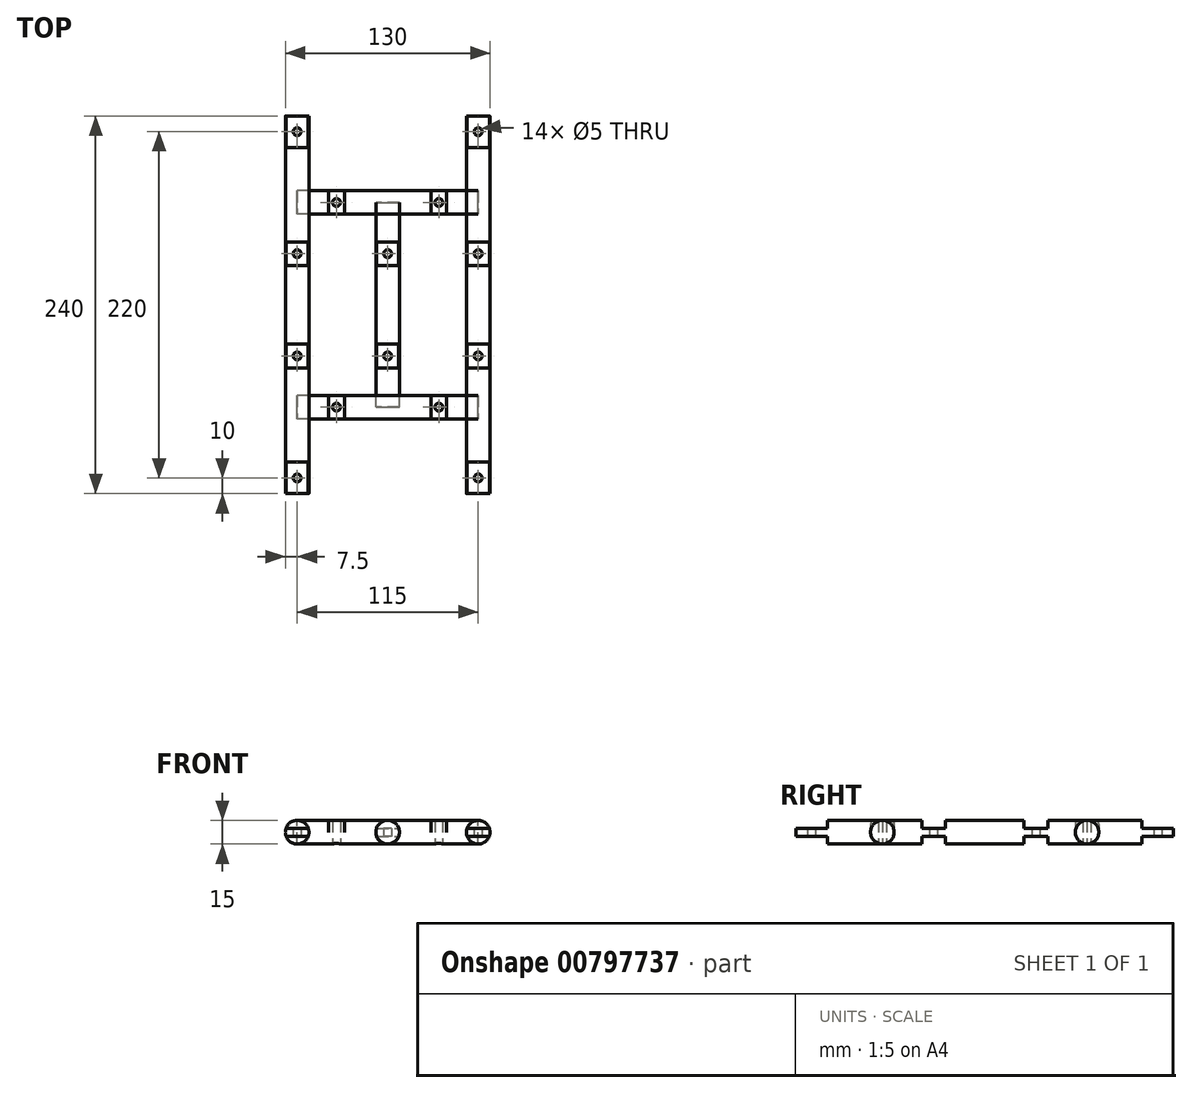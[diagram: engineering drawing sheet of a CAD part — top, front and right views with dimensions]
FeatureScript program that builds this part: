
annotation { "Feature Type Name" : "Feature", "Feature Type Description" : "" }
export const myFeature = defineFeature(function(context is Context, id is Id, definition is map)
    precondition{}
    {
        {
            var Q0;
            Q0=qCreatedBy(makeId("Top.planeOp"),FACE);
            var sketch = newSketch(context, id + "F0", { "sketchPlane" : qUnion([Q0])});
            skLineSegment(sketch, "E0.bottom", {"start": v(-65, 120) * mm, "end": v(-50, 120) * mm});
            skLineSegment(sketch, "E0.top", {"start": v(-65, -120) * mm, "end": v(-50, -120) * mm});
            skLineSegment(sketch, "E0.left", {"start": v(-65, 120) * mm, "end": v(-65, -120) * mm});
            skLineSegment(sketch, "E0.right", {"start": v(-50, 120) * mm, "end": v(-50, 65) * mm});
            skLineSegment(sketch, "E1.MirrorCS", {"start": v(65, 120) * mm, "end": v(50, 120) * mm});
            skLineSegment(sketch, "E2.MirrorCS", {"start": v(65, -120) * mm, "end": v(50, -120) * mm});
            skLineSegment(sketch, "E3.MirrorCS", {"start": v(65, 120) * mm, "end": v(65, -120) * mm});
            skLineSegment(sketch, "E4.MirrorCS", {"start": v(50, 120) * mm, "end": v(50, 65) * mm});
            skLineSegment(sketch, "E5.bottom", {"start": v(-50, -50) * mm, "end": v(50, -50) * mm});
            skLineSegment(sketch, "E5.top", {"start": v(-50, -65) * mm, "end": v(50, -65) * mm});
            skLineSegment(sketch, "E6.bottom", {"start": v(-50, 65) * mm, "end": v(50, 65) * mm});
            skLineSegment(sketch, "E6.top", {"start": v(-50, 50) * mm, "end": v(50, 50) * mm});
            skLineSegment(sketch, "E7", {"start": v(-57.5, -120) * mm, "end": v(-57.5, 120) * mm, "construction": true});
            skLineSegment(sketch, "E8", {"start": v(-50, -57.5) * mm, "end": v(50, -57.5) * mm, "construction": true});
            skLineSegment(sketch, "E9", {"start": v(-50, 57.5) * mm, "end": v(50, 57.5) * mm, "construction": true});
            skLineSegment(sketch, "E10", {"start": v(57.5, 120) * mm, "end": v(57.5, -120) * mm, "construction": true});
            skLineSegment(sketch, "E11.trimOffspring", {"start": v(-50, -65) * mm, "end": v(-50, -120) * mm});
            skLineSegment(sketch, "E12.trimOffspring", {"start": v(50, -65) * mm, "end": v(50, -120) * mm});
            skLineSegment(sketch, "E13.trimOffspring", {"start": v(-50, 50) * mm, "end": v(-50, -50) * mm});
            skLineSegment(sketch, "E14.trimOffspring", {"start": v(50, 50) * mm, "end": v(50, -50) * mm});
            skLineSegment(sketch, "E15", {"start": v(-57.5, 120) * mm, "end": v(57.5, 120) * mm, "construction": true});
            skLineSegment(sketch, "E16", {"start": v(-57.5, -120) * mm, "end": v(57.5, -120) * mm, "construction": true});
            skLineSegment(sketch, "E17", {"start": v(0, -120) * mm, "end": v(0, 120) * mm, "construction": true});
            skLineSegment(sketch, "E18.bottom", {"start": v(-7.5, -57.5) * mm, "end": v(7.5, -57.5) * mm});
            skLineSegment(sketch, "E18.top", {"start": v(-7.5, 57.5) * mm, "end": v(7.5, 57.5) * mm});
            skLineSegment(sketch, "E18.left", {"start": v(-7.5, -57.5) * mm, "end": v(-7.5, 57.5) * mm});
            skLineSegment(sketch, "E18.right", {"start": v(7.5, -57.5) * mm, "end": v(7.5, 57.5) * mm});
            skSolve(sketch);
        }
        {
            var Q0;
            {var subQ1=sQuery(id+"F0.wireOp",EDGE,"E0.bottom");Q0=makeQuery(id+"F0.imprint","IMPRINT",FACE,{"disambiguationData":[TD([[makeQuery(id+"F0.imprint","IMPRINT",EDGE,{"derivedFrom":subQ1}),-1.0]])]});}
            var Q1;
            Q1=makeQuery(id+"F0.imprint","IMPRINT",FACE,{"disambiguationData":[TD([[makeQuery(id+"F0.imprint","IMPRINT",EDGE,{"derivedFrom":sQuery(id+"F0.wireOp",EDGE,"E5.bottom")}),-1.0]])]});
            var Q2;
            {var subQ1=sQuery(id+"F0.wireOp",EDGE,"E1.MirrorCS");Q2=makeQuery(id+"F0.imprint","IMPRINT",FACE,{"disambiguationData":[TD([[makeQuery(id+"F0.imprint","IMPRINT",EDGE,{"derivedFrom":subQ1}),1.0]])]});}
            var Q3;
            Q3=makeQuery(id+"F0.imprint","IMPRINT",FACE,{"disambiguationData":[TD([[makeQuery(id+"F0.imprint","IMPRINT",EDGE,{"derivedFrom":sQuery(id+"F0.wireOp",EDGE,"E6.bottom")}),-1.0]])]});
            var Q4;
            {var subQ0=sQuery(id+"F0.wireOp",EDGE,"E18.left");var subQ1=sQuery(id+"F0.wireOp",EDGE,"E5.bottom");var subQ2=makeQuery(id+"F0.imprint","INTERSECT",VERTEX,{"derivedFrom":[subQ1,subQ0]});Q4=makeQuery(id+"F0.imprint","IMPRINT",FACE,{"disambiguationData":[TD([[makeQuery(id+"F0.imprint","IMPRINT",EDGE,{"disambiguationData":[TD([[subQ2,-1.0]])],"derivedFrom":subQ1}),1.0]])]});}
            var Q5;
            {var subQ5=sQuery(id+"F0.wireOp",EDGE,"E18.bottom");Q5=makeQuery(id+"F0.imprint","IMPRINT",FACE,{"disambiguationData":[TD([[makeQuery(id+"F0.imprint","IMPRINT",EDGE,{"derivedFrom":subQ5}),1.0]])]});}
            var Q6;
            {var subQ5=sQuery(id+"F0.wireOp",EDGE,"E18.top");Q6=makeQuery(id+"F0.imprint","IMPRINT",FACE,{"disambiguationData":[TD([[makeQuery(id+"F0.imprint","IMPRINT",EDGE,{"derivedFrom":subQ5}),-1.0]])]});}
            extrude(context, id + "F1", {"entities" : qUnion([Q0, Q1, Q2, Q3, Q4, Q5, Q6]), "depth" : 15 * mm, "offsetDistance" : 25 * mm});
        }
        {
            var Q0;
            Q0=qCreatedBy(makeId("Front.planeOp"),FACE);
            var sketch = newSketch(context, id + "F2", { "sketchPlane" : qUnion([Q0])});
            skLineSegment(sketch, "E19", {"start": v(0, 0) * mm, "end": v(57.99, 0) * mm, "construction": true});
            skLineSegment(sketch, "E20", {"start": v(0, 0) * mm, "end": v(0, 15) * mm, "construction": true});
            skLineSegment(sketch, "E21", {"start": v(-57.5, 7.5) * mm, "end": v(0, 7.5) * mm, "construction": true});
            skPoint(sketch, "E21.startSnap0", {"position": v(0, 7.5) * mm});
            skLineSegment(sketch, "E22", {"start": v(0, 7.5) * mm, "end": v(57.5, 7.5) * mm, "construction": true});
            skCircle(sketch, "E23", {"center": v(-57.5, 7.5) * mm, "radius": 7.5 * mm});
            skCircle(sketch, "E24", {"center": v(57.5, 7.5) * mm, "radius": 7.5 * mm});
            skCircle(sketch, "E25", {"center": v(0, 7.5) * mm, "radius": 7.5 * mm});
            skSolve(sketch);
        }
        {
            var Q0;
            Q0 = qSketchRegion(id + "F2", true);
            extrude(context, id + "F3", {"entities" : qUnion([Q0]), "operationType" : NewBodyOperationType.INTERSECT, "depth" : 125 * mm, "offsetDistance" : 25 * mm, "hasSecondDirection" : true, "secondDirectionOppositeDirection" : true, "secondDirectionDepth" : 125 * mm});
        }
        {
            var Q0;
            Q0=qCreatedBy(makeId("Right.planeOp"),FACE);
            var sketch = newSketch(context, id + "F4", { "sketchPlane" : qUnion([Q0])});
            skLineSegment(sketch, "E26", {"start": v(0, 0) * mm, "end": v(0, 15) * mm, "construction": true});
            skLineSegment(sketch, "E27", {"start": v(0, 7.5) * mm, "end": v(65, 7.5) * mm, "construction": true});
            skLineSegment(sketch, "E28", {"start": v(0, 7.5) * mm, "end": v(-65, 7.5) * mm, "construction": true});
            skCircle(sketch, "E29", {"center": v(65, 7.5) * mm, "radius": 7.5 * mm});
            skCircle(sketch, "E30", {"center": v(-65, 7.5) * mm, "radius": 7.5 * mm});
            skSolve(sketch);
        }
        {
            var Q0;
            Q0=makeQuery(id+"F4.imprint","IMPRINT",FACE,{"disambiguationData":[TD([[makeQuery(id+"F4.imprint","IMPRINT",EDGE,{"derivedFrom":sQuery(id+"F4.wireOp",EDGE,"E29")}),1.0]])]});
            var Q1;
            Q1=makeQuery(id+"F4.imprint","IMPRINT",FACE,{"disambiguationData":[TD([[makeQuery(id+"F4.imprint","IMPRINT",EDGE,{"derivedFrom":sQuery(id+"F4.wireOp",EDGE,"E30")}),1.0]])]});
            extrude(context, id + "F5", {"entities" : qUnion([Q0, Q1]), "depth" : 57.5 * mm, "offsetDistance" : 25 * mm, "hasSecondDirection" : true, "secondDirectionOppositeDirection" : true, "secondDirectionDepth" : 57.5 * mm});
        }
        {
            var Q0;
            Q0=qCreatedBy(makeId("Right.planeOp"),FACE);
            var sketch = newSketch(context, id + "F6", { "sketchPlane" : qUnion([Q0])});
            skLineSegment(sketch, "E31", {"start": v(0, 0) * mm, "end": v(0, 15) * mm, "construction": true});
            skLineSegment(sketch, "E32", {"start": v(120, 7.5) * mm, "end": v(-120, 7.5) * mm, "construction": true});
            skPoint(sketch, "E32.startSnap0", {"position": v(0, 7.5) * mm});
            skPoint(sketch, "E33", {"position": v(-110, 7.5) * mm});
            skPoint(sketch, "E34", {"position": v(-32.5, 7.5) * mm});
            skPoint(sketch, "E35", {"position": v(32.5, 7.5) * mm});
            skPoint(sketch, "E36", {"position": v(110, 7.5) * mm});
            skLineSegment(sketch, "E37.bottom", {"start": v(120, 10) * mm, "end": v(100, 10) * mm});
            skLineSegment(sketch, "E37.top", {"start": v(120, 5) * mm, "end": v(100, 5) * mm});
            skLineSegment(sketch, "E38.bottom", {"start": v(40, 10) * mm, "end": v(25, 10) * mm});
            skLineSegment(sketch, "E38.top", {"start": v(40, 5) * mm, "end": v(25, 5) * mm});
            skLineSegment(sketch, "E39.bottom", {"start": v(-25, 10) * mm, "end": v(-40, 10) * mm});
            skLineSegment(sketch, "E39.top", {"start": v(-25, 5) * mm, "end": v(-40, 5) * mm});
            skLineSegment(sketch, "E40.bottom", {"start": v(-100, 10) * mm, "end": v(-120, 10) * mm});
            skLineSegment(sketch, "E40.top", {"start": v(-100, 5) * mm, "end": v(-120, 5) * mm});
            skLineSegment(sketch, "E41.top", {"start": v(120, 15) * mm, "end": v(100, 15) * mm});
            skLineSegment(sketch, "E41.left", {"start": v(120, 10) * mm, "end": v(120, 15) * mm});
            skLineSegment(sketch, "E41.right", {"start": v(100, 10) * mm, "end": v(100, 15) * mm});
            skLineSegment(sketch, "E42.bottom", {"start": v(100, 5) * mm, "end": v(120, 5) * mm});
            skLineSegment(sketch, "E42.top", {"start": v(100, 0) * mm, "end": v(120, 0) * mm});
            skLineSegment(sketch, "E42.left", {"start": v(100, 5) * mm, "end": v(100, 0) * mm});
            skLineSegment(sketch, "E42.right", {"start": v(120, 5) * mm, "end": v(120, 0) * mm});
            skLineSegment(sketch, "E43.top", {"start": v(40, 0) * mm, "end": v(25, 0) * mm});
            skLineSegment(sketch, "E43.left", {"start": v(40, 5) * mm, "end": v(40, 0) * mm});
            skLineSegment(sketch, "E43.right", {"start": v(25, 5) * mm, "end": v(25, 0) * mm});
            skLineSegment(sketch, "E44.top", {"start": v(40, 15) * mm, "end": v(25, 15) * mm});
            skLineSegment(sketch, "E44.left", {"start": v(40, 10) * mm, "end": v(40, 15) * mm});
            skLineSegment(sketch, "E44.right", {"start": v(25, 10) * mm, "end": v(25, 15) * mm});
            skLineSegment(sketch, "E45.top", {"start": v(-25, 0) * mm, "end": v(-40, 0) * mm});
            skLineSegment(sketch, "E45.left", {"start": v(-25, 5) * mm, "end": v(-25, 0) * mm});
            skLineSegment(sketch, "E45.right", {"start": v(-40, 5) * mm, "end": v(-40, 0) * mm});
            skLineSegment(sketch, "E46.top", {"start": v(-25, 15) * mm, "end": v(-40, 15) * mm});
            skLineSegment(sketch, "E46.left", {"start": v(-25, 10) * mm, "end": v(-25, 15) * mm});
            skLineSegment(sketch, "E46.right", {"start": v(-40, 10) * mm, "end": v(-40, 15) * mm});
            skLineSegment(sketch, "E47.top", {"start": v(-100, 0) * mm, "end": v(-120, 0) * mm});
            skLineSegment(sketch, "E47.left", {"start": v(-100, 5) * mm, "end": v(-100, 0) * mm});
            skLineSegment(sketch, "E47.right", {"start": v(-120, 5) * mm, "end": v(-120, 0) * mm});
            skLineSegment(sketch, "E48.bottom", {"start": v(-120, 10) * mm, "end": v(-100, 10) * mm});
            skLineSegment(sketch, "E48.top", {"start": v(-120, 15) * mm, "end": v(-100, 15) * mm});
            skLineSegment(sketch, "E48.left", {"start": v(-120, 10) * mm, "end": v(-120, 15) * mm});
            skLineSegment(sketch, "E48.right", {"start": v(-100, 10) * mm, "end": v(-100, 15) * mm});
            skSolve(sketch);
        }
        {
            var Q0;
            Q0 = qSketchRegion(id + "F6", true);
            extrude(context, id + "F7", {"entities" : qUnion([Q0]), "operationType" : NewBodyOperationType.REMOVE, "oppositeDirection" : true, "depth" : 84.3 * mm, "offsetDistance" : 25 * mm, "hasSecondDirection" : true, "secondDirectionOppositeDirection" : false, "secondDirectionDepth" : 107 * mm});
        }
        {
            var Q0;
            Q0=qCreatedBy(makeId("Top.planeOp"),FACE);
            var sketch = newSketch(context, id + "F8", { "sketchPlane" : qUnion([Q0])});
            skLineSegment(sketch, "E49", {"start": v(-57.5, 0) * mm, "end": v(57.5, 0) * mm, "construction": true});
            skLineSegment(sketch, "E50", {"start": v(-57.5, 110) * mm, "end": v(-57.5, -110) * mm, "construction": true});
            skLineSegment(sketch, "E51", {"start": v(57.5, -110) * mm, "end": v(57.5, 110) * mm, "construction": true});
            skPoint(sketch, "E52", {"position": v(-57.5, -32.5) * mm});
            skPoint(sketch, "E53", {"position": v(57.5, -32.5) * mm});
            skPoint(sketch, "E54", {"position": v(57.5, 32.5) * mm});
            skPoint(sketch, "E55", {"position": v(-57.5, 32.5) * mm});
            skCircle(sketch, "E56", {"center": v(57.5, 110) * mm, "radius": 2.5 * mm});
            skCircle(sketch, "E57", {"center": v(57.5, 32.5) * mm, "radius": 2.5 * mm});
            skCircle(sketch, "E58", {"center": v(57.5, -32.5) * mm, "radius": 2.5 * mm});
            skCircle(sketch, "E59", {"center": v(57.5, -110) * mm, "radius": 2.5 * mm});
            skCircle(sketch, "E60", {"center": v(-57.5, -110) * mm, "radius": 2.5 * mm});
            skCircle(sketch, "E61", {"center": v(-57.5, -32.5) * mm, "radius": 2.5 * mm});
            skCircle(sketch, "E62", {"center": v(-57.5, 32.5) * mm, "radius": 2.5 * mm});
            skCircle(sketch, "E63", {"center": v(-57.5, 110) * mm, "radius": 2.5 * mm});
            skLineSegment(sketch, "E64", {"start": v(57.5, 32.5) * mm, "end": v(-57.5, 32.5) * mm, "construction": true});
            skLineSegment(sketch, "E65", {"start": v(57.5, -32.5) * mm, "end": v(-57.5, -32.5) * mm, "construction": true});
            skLineSegment(sketch, "E66", {"start": v(0, 32.5) * mm, "end": v(0, -32.5) * mm, "construction": true});
            skCircle(sketch, "E67", {"center": v(0, 32.5) * mm, "radius": 2.5 * mm});
            skCircle(sketch, "E68", {"center": v(0, -32.5) * mm, "radius": 2.5 * mm});
            skSolve(sketch);
        }
        {
            var Q0;
            Q0 = qSketchRegion(id + "F8", true);
            var Q1;
            Q1 = qSketchRegion(id + "F10", true);
            extrude(context, id + "F9", {"entities" : qUnion([Q0, Q1]), "operationType" : NewBodyOperationType.REMOVE, "depth" : 41.9 * mm, "offsetDistance" : 25 * mm});
        }
        {
            var Q0;
            Q0=qCreatedBy(makeId("Front.planeOp"),FACE);
            var sketch = newSketch(context, id + "F10", { "sketchPlane" : qUnion([Q0])});
            skLineSegment(sketch, "E69", {"start": v(0, 0) * mm, "end": v(0, 15) * mm, "construction": true});
            skLineSegment(sketch, "E70", {"start": v(0, 15) * mm, "end": v(-57.5, 15) * mm, "construction": true});
            skLineSegment(sketch, "E71", {"start": v(0, 15) * mm, "end": v(57.5, 15) * mm, "construction": true});
            skPoint(sketch, "E72", {"position": v(-27.5, 15) * mm});
            skPoint(sketch, "E73", {"position": v(-37.5, 15) * mm});
            skPoint(sketch, "E74", {"position": v(27.5, 15) * mm});
            skPoint(sketch, "E75", {"position": v(37.5, 15) * mm});
            skLineSegment(sketch, "E76.bottom", {"start": v(-37.5, 15) * mm, "end": v(-27.5, 15) * mm});
            skLineSegment(sketch, "E76.top", {"start": v(-37.5, 7.5) * mm, "end": v(-27.5, 7.5) * mm});
            skLineSegment(sketch, "E76.left", {"start": v(-37.5, 15) * mm, "end": v(-37.5, 7.5) * mm});
            skLineSegment(sketch, "E76.right", {"start": v(-27.5, 15) * mm, "end": v(-27.5, 7.5) * mm});
            skLineSegment(sketch, "E77.bottom", {"start": v(27.5, 15) * mm, "end": v(37.5, 15) * mm});
            skLineSegment(sketch, "E77.top", {"start": v(27.5, 7.5) * mm, "end": v(37.5, 7.5) * mm});
            skLineSegment(sketch, "E77.left", {"start": v(27.5, 15) * mm, "end": v(27.5, 7.5) * mm});
            skLineSegment(sketch, "E77.right", {"start": v(37.5, 15) * mm, "end": v(37.5, 7.5) * mm});
            skSolve(sketch);
        }
        {
            var Q0;
            Q0 = qSketchRegion(id + "F10", true);
            var Q1;
            Q1 = qSketchRegion(id + "F12", true);
            extrude(context, id + "F11", {"entities" : qUnion([Q0, Q1]), "operationType" : NewBodyOperationType.ADD, "depth" : 72.5 * mm, "offsetDistance" : 25 * mm, "hasSecondDirection" : true, "secondDirectionOppositeDirection" : true, "secondDirectionDepth" : 72.5 * mm});
        }
        {
            var Q0;
            Q0=qCreatedBy(makeId("Top.planeOp"),FACE);
            var sketch = newSketch(context, id + "F12", { "sketchPlane" : qUnion([Q0])});
            skLineSegment(sketch, "E78", {"start": v(-37.5, 0) * mm, "end": v(37.5, 0) * mm, "construction": true});
            skLineSegment(sketch, "E79", {"start": v(37.5, 57.5) * mm, "end": v(37.5, -57.5) * mm, "construction": true});
            skLineSegment(sketch, "E80.bottom", {"start": v(37.5, 57.5) * mm, "end": v(7.5, 57.5) * mm});
            skLineSegment(sketch, "E80.top", {"start": v(37.5, -57.5) * mm, "end": v(7.5, -57.5) * mm});
            skLineSegment(sketch, "E80.left", {"start": v(37.5, 57.5) * mm, "end": v(37.5, -57.5) * mm});
            skLineSegment(sketch, "E80.right", {"start": v(-37.5, 57.5) * mm, "end": v(-37.5, -57.5) * mm});
            skLineSegment(sketch, "E81", {"start": v(-32.5, 57.5) * mm, "end": v(-32.5, 65) * mm, "construction": true});
            skLineSegment(sketch, "E82", {"start": v(-32.5, -57.5) * mm, "end": v(-32.5, -65) * mm, "construction": true});
            skLineSegment(sketch, "E83", {"start": v(32.5, 57.5) * mm, "end": v(32.5, 65) * mm, "construction": true});
            skLineSegment(sketch, "E84", {"start": v(32.5, -57.5) * mm, "end": v(32.5, -65) * mm, "construction": true});
            skCircle(sketch, "E85", {"center": v(-32.5, -65) * mm, "radius": 2.5 * mm});
            skCircle(sketch, "E86", {"center": v(32.5, -65) * mm, "radius": 2.5 * mm});
            skCircle(sketch, "E87", {"center": v(32.5, 65) * mm, "radius": 2.5 * mm});
            skCircle(sketch, "E88", {"center": v(-32.5, 65) * mm, "radius": 2.5 * mm});
            skLineSegment(sketch, "E89", {"start": v(7.5, -57.5) * mm, "end": v(7.5, 57.5) * mm});
            skLineSegment(sketch, "E90", {"start": v(-7.5, -57.5) * mm, "end": v(-7.5, 57.5) * mm});
            skLineSegment(sketch, "E91.trimOffspring", {"start": v(-7.5, -57.5) * mm, "end": v(-37.5, -57.5) * mm});
            skLineSegment(sketch, "E92.trimOffspring", {"start": v(-7.5, 57.5) * mm, "end": v(-37.5, 57.5) * mm});
            skSolve(sketch);
        }
        {
            var Q0;
            Q0 = qSketchRegion(id + "F12", true);
            extrude(context, id + "F13", {"entities" : qUnion([Q0]), "operationType" : NewBodyOperationType.REMOVE, "depth" : 25 * mm, "offsetDistance" : 25 * mm});
        }
        {
            var Q0;
            Q0=makeQuery(id+"F7.boolean.opBoolean","INTERSECT",EDGE,{"disambiguationData":[OD(1.0)],"derivedFrom":[makeQuery(id+"F3.boolean.opBoolean","COPY",FACE,{"derivedFrom":makeQuery(id+"F3.boolean.toolComplement.opBoolean","COPY",FACE,{"derivedFrom":makeQuery(id+"F3.opExtrude","SWEPT_FACE",FACE,{"disambiguationData":[OSD([sQuery(id+"F2.wireOp",EDGE,"E24")])]})})}),makeQuery(id+"F7.opExtrude","SWEPT_FACE",FACE,{"disambiguationData":[OSD([sQuery(id+"F6.wireOp",EDGE,"E48.bottom")])]})]});
            var Q1;
            Q1=makeQuery(id+"F7.boolean.opBoolean","INTERSECT",EDGE,{"disambiguationData":[OD(0.0)],"derivedFrom":[makeQuery(id+"F3.boolean.opBoolean","COPY",FACE,{"derivedFrom":makeQuery(id+"F3.boolean.toolComplement.opBoolean","COPY",FACE,{"derivedFrom":makeQuery(id+"F3.opExtrude","SWEPT_FACE",FACE,{"disambiguationData":[OSD([sQuery(id+"F2.wireOp",EDGE,"E24")])]})})}),makeQuery(id+"F7.opExtrude","SWEPT_FACE",FACE,{"disambiguationData":[OSD([sQuery(id+"F6.wireOp",EDGE,"E48.bottom")])]})]});
            var Q2;
            Q2=makeQuery(id+"F13.boolean.opBoolean","INTERSECT",EDGE,{"derivedFrom":[makeQuery(id+"F11.opExtrude","SWEPT_FACE",FACE,{"disambiguationData":[OSD([sQuery(id+"F10.wireOp",EDGE,"E77.bottom")])]}),makeQuery(id+"F13.opExtrude","SWEPT_FACE",FACE,{"disambiguationData":[OSD([sQuery(id+"F12.wireOp",EDGE,"E80.top")])]})]});
            var Q3;
            Q3=makeQuery(id+"F7.boolean.opBoolean","INTERSECT",EDGE,{"disambiguationData":[OD(0.0)],"derivedFrom":[makeQuery(id+"F3.boolean.opBoolean","COPY",FACE,{"derivedFrom":makeQuery(id+"F3.boolean.toolComplement.opBoolean","COPY",FACE,{"derivedFrom":makeQuery(id+"F3.opExtrude","SWEPT_FACE",FACE,{"disambiguationData":[OSD([sQuery(id+"F2.wireOp",EDGE,"E24")])]})})}),makeQuery(id+"F7.opExtrude","SWEPT_FACE",FACE,{"disambiguationData":[OSD([sQuery(id+"F6.wireOp",EDGE,"E39.bottom")])]})]});
            var Q4;
            Q4=makeQuery(id+"F11.opExtrude","CAP_EDGE",EDGE,{"disambiguationData":[OSD([sQuery(id+"F10.wireOp",EDGE,"E77.bottom")])],"isStart":false});
            var Q5;
            Q5=makeQuery(id+"F7.boolean.opBoolean","INTERSECT",EDGE,{"disambiguationData":[OD(1.0)],"derivedFrom":[makeQuery(id+"F3.boolean.opBoolean","COPY",FACE,{"derivedFrom":makeQuery(id+"F3.boolean.toolComplement.opBoolean","COPY",FACE,{"derivedFrom":makeQuery(id+"F3.opExtrude","SWEPT_FACE",FACE,{"disambiguationData":[OSD([sQuery(id+"F2.wireOp",EDGE,"E24")])]})})}),makeQuery(id+"F7.opExtrude","SWEPT_FACE",FACE,{"disambiguationData":[OSD([sQuery(id+"F6.wireOp",EDGE,"E39.bottom")])]})]});
            var Q6;
            Q6=makeQuery(id+"F7.boolean.opBoolean","INTERSECT",EDGE,{"disambiguationData":[OD(1.0)],"derivedFrom":[makeQuery(id+"F3.boolean.opBoolean","COPY",FACE,{"derivedFrom":makeQuery(id+"F3.boolean.toolComplement.opBoolean","COPY",FACE,{"derivedFrom":makeQuery(id+"F3.opExtrude","SWEPT_FACE",FACE,{"disambiguationData":[OSD([sQuery(id+"F2.wireOp",EDGE,"E24")])]})})}),makeQuery(id+"F7.opExtrude","SWEPT_FACE",FACE,{"disambiguationData":[OSD([sQuery(id+"F6.wireOp",EDGE,"E38.bottom")])]})]});
            var Q7;
            Q7=makeQuery(id+"F7.boolean.opBoolean","INTERSECT",EDGE,{"disambiguationData":[OD(0.0)],"derivedFrom":[makeQuery(id+"F3.boolean.opBoolean","COPY",FACE,{"derivedFrom":makeQuery(id+"F3.boolean.toolComplement.opBoolean","COPY",FACE,{"derivedFrom":makeQuery(id+"F3.opExtrude","SWEPT_FACE",FACE,{"disambiguationData":[OSD([sQuery(id+"F2.wireOp",EDGE,"E24")])]})})}),makeQuery(id+"F7.opExtrude","SWEPT_FACE",FACE,{"disambiguationData":[OSD([sQuery(id+"F6.wireOp",EDGE,"E38.bottom")])]})]});
            var Q8;
            Q8=makeQuery(id+"F7.boolean.opBoolean","INTERSECT",EDGE,{"disambiguationData":[OD(1.0)],"derivedFrom":[makeQuery(id+"F3.boolean.opBoolean","COPY",FACE,{"derivedFrom":makeQuery(id+"F3.boolean.toolComplement.opBoolean","COPY",FACE,{"derivedFrom":makeQuery(id+"F3.opExtrude","SWEPT_FACE",FACE,{"disambiguationData":[OSD([sQuery(id+"F2.wireOp",EDGE,"E24")])]})})}),makeQuery(id+"F7.opExtrude","SWEPT_FACE",FACE,{"disambiguationData":[OSD([sQuery(id+"F6.wireOp",EDGE,"E37.bottom")])]})]});
            var Q9;
            Q9=makeQuery(id+"F7.boolean.opBoolean","INTERSECT",EDGE,{"disambiguationData":[OD(0.0)],"derivedFrom":[makeQuery(id+"F3.boolean.opBoolean","COPY",FACE,{"derivedFrom":makeQuery(id+"F3.boolean.toolComplement.opBoolean","COPY",FACE,{"derivedFrom":makeQuery(id+"F3.opExtrude","SWEPT_FACE",FACE,{"disambiguationData":[OSD([sQuery(id+"F2.wireOp",EDGE,"E24")])]})})}),makeQuery(id+"F7.opExtrude","SWEPT_FACE",FACE,{"disambiguationData":[OSD([sQuery(id+"F6.wireOp",EDGE,"E37.bottom")])]})]});
            var Q10;
            Q10=makeQuery(id+"F11.opExtrude","CAP_EDGE",EDGE,{"disambiguationData":[OSD([sQuery(id+"F10.wireOp",EDGE,"E77.bottom")])],"isStart":true});
            var Q11;
            Q11=makeQuery(id+"F13.boolean.opBoolean","INTERSECT",EDGE,{"derivedFrom":[makeQuery(id+"F11.opExtrude","SWEPT_FACE",FACE,{"disambiguationData":[OSD([sQuery(id+"F10.wireOp",EDGE,"E77.bottom")])]}),makeQuery(id+"F13.opExtrude","SWEPT_FACE",FACE,{"disambiguationData":[OSD([sQuery(id+"F12.wireOp",EDGE,"E80.bottom")])]})]});
            var Q12;
            Q12=makeQuery(id+"F13.boolean.opBoolean","INTERSECT",EDGE,{"derivedFrom":[makeQuery(id+"F11.opExtrude","SWEPT_FACE",FACE,{"disambiguationData":[OSD([sQuery(id+"F10.wireOp",EDGE,"E76.bottom")])]}),makeQuery(id+"F13.opExtrude","SWEPT_FACE",FACE,{"disambiguationData":[OSD([sQuery(id+"F12.wireOp",EDGE,"E80.top")])]})]});
            var Q13;
            Q13=makeQuery(id+"F11.opExtrude","CAP_EDGE",EDGE,{"disambiguationData":[OSD([sQuery(id+"F10.wireOp",EDGE,"E76.bottom")])],"isStart":false});
            var Q14;
            Q14=makeQuery(id+"F13.boolean.opBoolean","INTERSECT",EDGE,{"derivedFrom":[makeQuery(id+"F11.opExtrude","SWEPT_FACE",FACE,{"disambiguationData":[OSD([sQuery(id+"F10.wireOp",EDGE,"E76.bottom")])]}),makeQuery(id+"F13.opExtrude","SWEPT_FACE",FACE,{"disambiguationData":[OSD([sQuery(id+"F12.wireOp",EDGE,"E80.bottom")])]})]});
            var Q15;
            Q15=makeQuery(id+"F11.opExtrude","CAP_EDGE",EDGE,{"disambiguationData":[OSD([sQuery(id+"F10.wireOp",EDGE,"E76.bottom")])],"isStart":true});
            var Q16;
            Q16=makeQuery(id+"F7.boolean.opBoolean","INTERSECT",EDGE,{"disambiguationData":[OD(0.0)],"derivedFrom":[makeQuery(id+"F3.boolean.opBoolean","COPY",FACE,{"derivedFrom":makeQuery(id+"F3.boolean.toolComplement.opBoolean","COPY",FACE,{"derivedFrom":makeQuery(id+"F3.opExtrude","SWEPT_FACE",FACE,{"disambiguationData":[OSD([sQuery(id+"F2.wireOp",EDGE,"E23")])]})})}),makeQuery(id+"F7.opExtrude","SWEPT_FACE",FACE,{"disambiguationData":[OSD([sQuery(id+"F6.wireOp",EDGE,"E37.bottom")])]})]});
            var Q17;
            Q17=makeQuery(id+"F7.boolean.opBoolean","INTERSECT",EDGE,{"disambiguationData":[OD(1.0)],"derivedFrom":[makeQuery(id+"F3.boolean.opBoolean","COPY",FACE,{"derivedFrom":makeQuery(id+"F3.boolean.toolComplement.opBoolean","COPY",FACE,{"derivedFrom":makeQuery(id+"F3.opExtrude","SWEPT_FACE",FACE,{"disambiguationData":[OSD([sQuery(id+"F2.wireOp",EDGE,"E23")])]})})}),makeQuery(id+"F7.opExtrude","SWEPT_FACE",FACE,{"disambiguationData":[OSD([sQuery(id+"F6.wireOp",EDGE,"E37.bottom")])]})]});
            var Q18;
            Q18=makeQuery(id+"F7.boolean.opBoolean","INTERSECT",EDGE,{"disambiguationData":[OD(1.0)],"derivedFrom":[makeQuery(id+"F3.boolean.opBoolean","COPY",FACE,{"derivedFrom":makeQuery(id+"F3.boolean.toolComplement.opBoolean","COPY",FACE,{"derivedFrom":makeQuery(id+"F3.opExtrude","SWEPT_FACE",FACE,{"disambiguationData":[OSD([sQuery(id+"F2.wireOp",EDGE,"E23")])]})})}),makeQuery(id+"F7.opExtrude","SWEPT_FACE",FACE,{"disambiguationData":[OSD([sQuery(id+"F6.wireOp",EDGE,"E38.bottom")])]})]});
            var Q19;
            Q19=makeQuery(id+"F7.boolean.opBoolean","INTERSECT",EDGE,{"disambiguationData":[OD(0.0)],"derivedFrom":[makeQuery(id+"F3.boolean.opBoolean","COPY",FACE,{"derivedFrom":makeQuery(id+"F3.boolean.toolComplement.opBoolean","COPY",FACE,{"derivedFrom":makeQuery(id+"F3.opExtrude","SWEPT_FACE",FACE,{"disambiguationData":[OSD([sQuery(id+"F2.wireOp",EDGE,"E23")])]})})}),makeQuery(id+"F7.opExtrude","SWEPT_FACE",FACE,{"disambiguationData":[OSD([sQuery(id+"F6.wireOp",EDGE,"E38.bottom")])]})]});
            var Q20;
            Q20=makeQuery(id+"F7.boolean.opBoolean","INTERSECT",EDGE,{"disambiguationData":[OD(0.0)],"derivedFrom":[makeQuery(id+"F3.boolean.opBoolean","COPY",FACE,{"derivedFrom":makeQuery(id+"F3.boolean.toolComplement.opBoolean","COPY",FACE,{"derivedFrom":makeQuery(id+"F3.opExtrude","SWEPT_FACE",FACE,{"disambiguationData":[OSD([sQuery(id+"F2.wireOp",EDGE,"E23")])]})})}),makeQuery(id+"F7.opExtrude","SWEPT_FACE",FACE,{"disambiguationData":[OSD([sQuery(id+"F6.wireOp",EDGE,"E39.bottom")])]})]});
            var Q21;
            Q21=makeQuery(id+"F7.boolean.opBoolean","INTERSECT",EDGE,{"disambiguationData":[OD(1.0)],"derivedFrom":[makeQuery(id+"F3.boolean.opBoolean","COPY",FACE,{"derivedFrom":makeQuery(id+"F3.boolean.toolComplement.opBoolean","COPY",FACE,{"derivedFrom":makeQuery(id+"F3.opExtrude","SWEPT_FACE",FACE,{"disambiguationData":[OSD([sQuery(id+"F2.wireOp",EDGE,"E23")])]})})}),makeQuery(id+"F7.opExtrude","SWEPT_FACE",FACE,{"disambiguationData":[OSD([sQuery(id+"F6.wireOp",EDGE,"E39.bottom")])]})]});
            var Q22;
            Q22=makeQuery(id+"F7.boolean.opBoolean","INTERSECT",EDGE,{"disambiguationData":[OD(1.0)],"derivedFrom":[makeQuery(id+"F3.boolean.opBoolean","COPY",FACE,{"derivedFrom":makeQuery(id+"F3.boolean.toolComplement.opBoolean","COPY",FACE,{"derivedFrom":makeQuery(id+"F3.opExtrude","SWEPT_FACE",FACE,{"disambiguationData":[OSD([sQuery(id+"F2.wireOp",EDGE,"E23")])]})})}),makeQuery(id+"F7.opExtrude","SWEPT_FACE",FACE,{"disambiguationData":[OSD([sQuery(id+"F6.wireOp",EDGE,"E48.bottom")])]})]});
            var Q23;
            Q23=makeQuery(id+"F7.boolean.opBoolean","INTERSECT",EDGE,{"disambiguationData":[OD(0.0)],"derivedFrom":[makeQuery(id+"F3.boolean.opBoolean","COPY",FACE,{"derivedFrom":makeQuery(id+"F3.boolean.toolComplement.opBoolean","COPY",FACE,{"derivedFrom":makeQuery(id+"F3.opExtrude","SWEPT_FACE",FACE,{"disambiguationData":[OSD([sQuery(id+"F2.wireOp",EDGE,"E23")])]})})}),makeQuery(id+"F7.opExtrude","SWEPT_FACE",FACE,{"disambiguationData":[OSD([sQuery(id+"F6.wireOp",EDGE,"E48.bottom")])]})]});
            var Q24;
            Q24=makeQuery(id+"F7.boolean.opBoolean","INTERSECT",EDGE,{"disambiguationData":[OD(1.0)],"derivedFrom":[makeQuery(id+"F3.boolean.opBoolean","COPY",FACE,{"derivedFrom":makeQuery(id+"F3.boolean.toolComplement.opBoolean","COPY",FACE,{"derivedFrom":makeQuery(id+"F3.opExtrude","SWEPT_FACE",FACE,{"disambiguationData":[OSD([sQuery(id+"F2.wireOp",EDGE,"E23")])]})})}),makeQuery(id+"F7.opExtrude","SWEPT_FACE",FACE,{"disambiguationData":[OSD([sQuery(id+"F6.wireOp",EDGE,"E40.top")])]})]});
            var Q25;
            Q25=makeQuery(id+"F7.boolean.opBoolean","INTERSECT",EDGE,{"disambiguationData":[OD(0.0)],"derivedFrom":[makeQuery(id+"F3.boolean.opBoolean","COPY",FACE,{"derivedFrom":makeQuery(id+"F3.boolean.toolComplement.opBoolean","COPY",FACE,{"derivedFrom":makeQuery(id+"F3.opExtrude","SWEPT_FACE",FACE,{"disambiguationData":[OSD([sQuery(id+"F2.wireOp",EDGE,"E23")])]})})}),makeQuery(id+"F7.opExtrude","SWEPT_FACE",FACE,{"disambiguationData":[OSD([sQuery(id+"F6.wireOp",EDGE,"E40.top")])]})]});
            var Q26;
            Q26=makeQuery(id+"F7.boolean.opBoolean","INTERSECT",EDGE,{"disambiguationData":[OD(0.0)],"derivedFrom":[makeQuery(id+"F3.boolean.opBoolean","COPY",FACE,{"derivedFrom":makeQuery(id+"F3.boolean.toolComplement.opBoolean","COPY",FACE,{"derivedFrom":makeQuery(id+"F3.opExtrude","SWEPT_FACE",FACE,{"disambiguationData":[OSD([sQuery(id+"F2.wireOp",EDGE,"E23")])]})})}),makeQuery(id+"F7.opExtrude","SWEPT_FACE",FACE,{"disambiguationData":[OSD([sQuery(id+"F6.wireOp",EDGE,"E39.top")])]})]});
            var Q27;
            Q27=makeQuery(id+"F7.boolean.opBoolean","INTERSECT",EDGE,{"disambiguationData":[OD(1.0)],"derivedFrom":[makeQuery(id+"F3.boolean.opBoolean","COPY",FACE,{"derivedFrom":makeQuery(id+"F3.boolean.toolComplement.opBoolean","COPY",FACE,{"derivedFrom":makeQuery(id+"F3.opExtrude","SWEPT_FACE",FACE,{"disambiguationData":[OSD([sQuery(id+"F2.wireOp",EDGE,"E23")])]})})}),makeQuery(id+"F7.opExtrude","SWEPT_FACE",FACE,{"disambiguationData":[OSD([sQuery(id+"F6.wireOp",EDGE,"E39.top")])]})]});
            var Q28;
            Q28=makeQuery(id+"F7.boolean.opBoolean","INTERSECT",EDGE,{"disambiguationData":[OD(0.0)],"derivedFrom":[makeQuery(id+"F3.boolean.opBoolean","COPY",FACE,{"derivedFrom":makeQuery(id+"F3.boolean.toolComplement.opBoolean","COPY",FACE,{"derivedFrom":makeQuery(id+"F3.opExtrude","SWEPT_FACE",FACE,{"disambiguationData":[OSD([sQuery(id+"F2.wireOp",EDGE,"E23")])]})})}),makeQuery(id+"F7.opExtrude","SWEPT_FACE",FACE,{"disambiguationData":[OSD([sQuery(id+"F6.wireOp",EDGE,"E38.top")])]})]});
            var Q29;
            Q29=makeQuery(id+"F7.boolean.opBoolean","INTERSECT",EDGE,{"disambiguationData":[OD(1.0)],"derivedFrom":[makeQuery(id+"F3.boolean.opBoolean","COPY",FACE,{"derivedFrom":makeQuery(id+"F3.boolean.toolComplement.opBoolean","COPY",FACE,{"derivedFrom":makeQuery(id+"F3.opExtrude","SWEPT_FACE",FACE,{"disambiguationData":[OSD([sQuery(id+"F2.wireOp",EDGE,"E23")])]})})}),makeQuery(id+"F7.opExtrude","SWEPT_FACE",FACE,{"disambiguationData":[OSD([sQuery(id+"F6.wireOp",EDGE,"E38.top")])]})]});
            var Q30;
            Q30=makeQuery(id+"F7.boolean.opBoolean","INTERSECT",EDGE,{"disambiguationData":[OD(0.0)],"derivedFrom":[makeQuery(id+"F3.boolean.opBoolean","COPY",FACE,{"derivedFrom":makeQuery(id+"F3.boolean.toolComplement.opBoolean","COPY",FACE,{"derivedFrom":makeQuery(id+"F3.opExtrude","SWEPT_FACE",FACE,{"disambiguationData":[OSD([sQuery(id+"F2.wireOp",EDGE,"E24")])]})})}),makeQuery(id+"F7.opExtrude","SWEPT_FACE",FACE,{"disambiguationData":[OSD([sQuery(id+"F6.wireOp",EDGE,"E40.top")])]})]});
            var Q31;
            Q31=makeQuery(id+"F7.boolean.opBoolean","INTERSECT",EDGE,{"disambiguationData":[OD(1.0)],"derivedFrom":[makeQuery(id+"F3.boolean.opBoolean","COPY",FACE,{"derivedFrom":makeQuery(id+"F3.boolean.toolComplement.opBoolean","COPY",FACE,{"derivedFrom":makeQuery(id+"F3.opExtrude","SWEPT_FACE",FACE,{"disambiguationData":[OSD([sQuery(id+"F2.wireOp",EDGE,"E24")])]})})}),makeQuery(id+"F7.opExtrude","SWEPT_FACE",FACE,{"disambiguationData":[OSD([sQuery(id+"F6.wireOp",EDGE,"E40.top")])]})]});
            var Q32;
            Q32=makeQuery(id+"F7.boolean.opBoolean","INTERSECT",EDGE,{"disambiguationData":[OD(0.0)],"derivedFrom":[makeQuery(id+"F3.boolean.opBoolean","COPY",FACE,{"derivedFrom":makeQuery(id+"F3.boolean.toolComplement.opBoolean","COPY",FACE,{"derivedFrom":makeQuery(id+"F3.opExtrude","SWEPT_FACE",FACE,{"disambiguationData":[OSD([sQuery(id+"F2.wireOp",EDGE,"E24")])]})})}),makeQuery(id+"F7.opExtrude","SWEPT_FACE",FACE,{"disambiguationData":[OSD([sQuery(id+"F6.wireOp",EDGE,"E39.top")])]})]});
            var Q33;
            Q33=makeQuery(id+"F7.boolean.opBoolean","INTERSECT",EDGE,{"disambiguationData":[OD(1.0)],"derivedFrom":[makeQuery(id+"F3.boolean.opBoolean","COPY",FACE,{"derivedFrom":makeQuery(id+"F3.boolean.toolComplement.opBoolean","COPY",FACE,{"derivedFrom":makeQuery(id+"F3.opExtrude","SWEPT_FACE",FACE,{"disambiguationData":[OSD([sQuery(id+"F2.wireOp",EDGE,"E24")])]})})}),makeQuery(id+"F7.opExtrude","SWEPT_FACE",FACE,{"disambiguationData":[OSD([sQuery(id+"F6.wireOp",EDGE,"E39.top")])]})]});
            var Q34;
            Q34=makeQuery(id+"F7.boolean.opBoolean","INTERSECT",EDGE,{"disambiguationData":[OD(0.0)],"derivedFrom":[makeQuery(id+"F3.boolean.opBoolean","COPY",FACE,{"derivedFrom":makeQuery(id+"F3.boolean.toolComplement.opBoolean","COPY",FACE,{"derivedFrom":makeQuery(id+"F3.opExtrude","SWEPT_FACE",FACE,{"disambiguationData":[OSD([sQuery(id+"F2.wireOp",EDGE,"E24")])]})})}),makeQuery(id+"F7.opExtrude","SWEPT_FACE",FACE,{"disambiguationData":[OSD([sQuery(id+"F6.wireOp",EDGE,"E38.top")])]})]});
            var Q35;
            Q35=makeQuery(id+"F7.boolean.opBoolean","INTERSECT",EDGE,{"disambiguationData":[OD(1.0)],"derivedFrom":[makeQuery(id+"F3.boolean.opBoolean","COPY",FACE,{"derivedFrom":makeQuery(id+"F3.boolean.toolComplement.opBoolean","COPY",FACE,{"derivedFrom":makeQuery(id+"F3.opExtrude","SWEPT_FACE",FACE,{"disambiguationData":[OSD([sQuery(id+"F2.wireOp",EDGE,"E24")])]})})}),makeQuery(id+"F7.opExtrude","SWEPT_FACE",FACE,{"disambiguationData":[OSD([sQuery(id+"F6.wireOp",EDGE,"E38.top")])]})]});
            var Q36;
            Q36=makeQuery(id+"F7.boolean.opBoolean","INTERSECT",EDGE,{"disambiguationData":[OD(0.0)],"derivedFrom":[makeQuery(id+"F3.boolean.opBoolean","COPY",FACE,{"derivedFrom":makeQuery(id+"F3.boolean.toolComplement.opBoolean","COPY",FACE,{"derivedFrom":makeQuery(id+"F3.opExtrude","SWEPT_FACE",FACE,{"disambiguationData":[OSD([sQuery(id+"F2.wireOp",EDGE,"E24")])]})})}),makeQuery(id+"F7.opExtrude","SWEPT_FACE",FACE,{"disambiguationData":[OSD([sQuery(id+"F6.wireOp",EDGE,"E42.bottom")])]})]});
            var Q37;
            Q37=makeQuery(id+"F7.boolean.opBoolean","INTERSECT",EDGE,{"disambiguationData":[OD(1.0)],"derivedFrom":[makeQuery(id+"F3.boolean.opBoolean","COPY",FACE,{"derivedFrom":makeQuery(id+"F3.boolean.toolComplement.opBoolean","COPY",FACE,{"derivedFrom":makeQuery(id+"F3.opExtrude","SWEPT_FACE",FACE,{"disambiguationData":[OSD([sQuery(id+"F2.wireOp",EDGE,"E24")])]})})}),makeQuery(id+"F7.opExtrude","SWEPT_FACE",FACE,{"disambiguationData":[OSD([sQuery(id+"F6.wireOp",EDGE,"E42.bottom")])]})]});
            var Q38;
            Q38=makeQuery(id+"F7.boolean.opBoolean","INTERSECT",EDGE,{"disambiguationData":[OD(1.0)],"derivedFrom":[makeQuery(id+"F3.boolean.opBoolean","COPY",FACE,{"derivedFrom":makeQuery(id+"F3.boolean.toolComplement.opBoolean","COPY",FACE,{"derivedFrom":makeQuery(id+"F3.opExtrude","SWEPT_FACE",FACE,{"disambiguationData":[OSD([sQuery(id+"F2.wireOp",EDGE,"E23")])]})})}),makeQuery(id+"F7.opExtrude","SWEPT_FACE",FACE,{"disambiguationData":[OSD([sQuery(id+"F6.wireOp",EDGE,"E42.bottom")])]})]});
            var Q39;
            Q39=makeQuery(id+"F7.boolean.opBoolean","INTERSECT",EDGE,{"disambiguationData":[OD(0.0)],"derivedFrom":[makeQuery(id+"F3.boolean.opBoolean","COPY",FACE,{"derivedFrom":makeQuery(id+"F3.boolean.toolComplement.opBoolean","COPY",FACE,{"derivedFrom":makeQuery(id+"F3.opExtrude","SWEPT_FACE",FACE,{"disambiguationData":[OSD([sQuery(id+"F2.wireOp",EDGE,"E23")])]})})}),makeQuery(id+"F7.opExtrude","SWEPT_FACE",FACE,{"disambiguationData":[OSD([sQuery(id+"F6.wireOp",EDGE,"E42.bottom")])]})]});
            fillet(context, id + "F14", {"entities" : qUnion([Q0, Q1, Q2, Q3, Q4, Q5, Q6, Q7, Q8, Q9, Q10, Q11, Q12, Q13, Q14, Q15, Q16, Q17, Q18, Q19, Q20, Q21, Q22, Q23, Q24, Q25, Q26, Q27, Q28, Q29, Q30, Q31, Q32, Q33, Q34, Q35, Q36, Q37, Q38, Q39]), "radius" : 2.5 * mm, "tangentPropagation" : true, "allowEdgeOverflow" : false});
        }
    });
